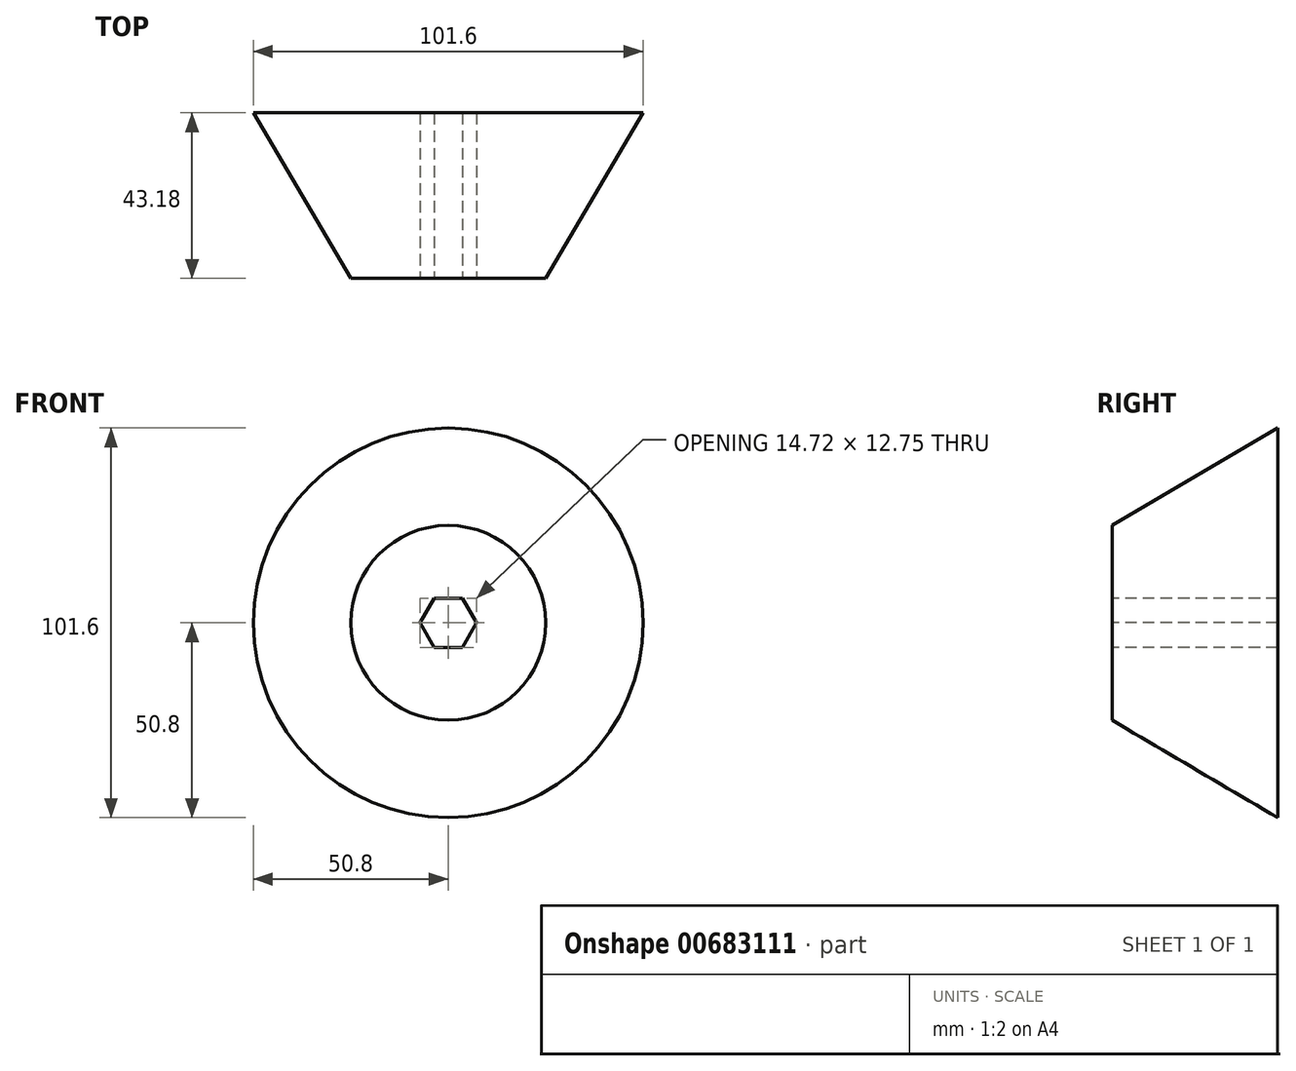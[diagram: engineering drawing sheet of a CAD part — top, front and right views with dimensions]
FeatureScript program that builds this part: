
annotation { "Feature Type Name" : "Feature", "Feature Type Description" : "" }
export const myFeature = defineFeature(function(context is Context, id is Id, definition is map)
    precondition{}
    {
        {
            var Q0;
            Q0=qCreatedBy(makeId("Front.planeOp"),FACE);
            var sketch = newSketch(context, id + "F0", { "sketchPlane" : qUnion([Q0])});
            skCircle(sketch, "E0", {"center": v(0, 0) * mm, "radius": 50.8 * mm});
            skSolve(sketch);
        }
        {
            var Q0;
            Q0=makeQuery(id+"F0.imprint","IMPRINT",FACE,{"disambiguationData":[TD([[makeQuery(id+"F0.imprint","IMPRINT",EDGE,{"derivedFrom":sQuery(id+"F0.wireOp",EDGE,"E0")}),1.0]])]});
            cPlane(context, id + "F1", {"entities" : qUnion([Q0]), "cplaneType" : CPlaneType.OFFSET, "offset" : 43.18 * mm, "width" : 152.4 * mm, "height" : 152.4 * mm});
        }
        {
            var Q0;
            Q0=qCreatedBy(id+"F1.planeOp",FACE);
            var sketch = newSketch(context, id + "F2", { "sketchPlane" : qUnion([Q0])});
            skCircle(sketch, "E1", {"center": v(0, 0) * mm, "radius": 25.4 * mm});
            skSolve(sketch);
        }
        {
            var Q0;
            Q0=makeQuery(id+"F0.imprint","IMPRINT",FACE,{"disambiguationData":[TD([[makeQuery(id+"F0.imprint","IMPRINT",EDGE,{"derivedFrom":sQuery(id+"F0.wireOp",EDGE,"E0")}),1.0]])]});
            var Q1;
            Q1=makeQuery(id+"F2.imprint","IMPRINT",FACE,{"disambiguationData":[TD([[makeQuery(id+"F2.imprint","IMPRINT",EDGE,{"derivedFrom":sQuery(id+"F2.wireOp",EDGE,"E1")}),1.0]])]});
            loft(context, id + "F3", {"sheetProfilesArray" : [{ "sheetProfileEntities" : qUnion([Q0]) }, { "sheetProfileEntities" : qUnion([Q1]) }]});
        }
        {
            var Q0;
            Q0=makeQuery(id+"F3.opLoft","CAP_FACE",FACE,{"disambiguationData":[OSD([makeQuery(id+"F2.imprint","IMPRINT",FACE,{"disambiguationData":[TD([[makeQuery(id+"F2.imprint","IMPRINT",EDGE,{"derivedFrom":sQuery(id+"F2.wireOp",EDGE,"E1")}),1.0]])]})])],"isStart":true});
            var sketch = newSketch(context, id + "F4", { "sketchPlane" : qUnion([Q0])});
            skCircle(sketch, "E2.cCircle", {"center": v(0, 0) * mm, "radius": 6.38 * mm, "construction": true});
            skLineSegment(sketch, "E2.0", {"start": v(3.68, -6.38) * mm, "end": v(-3.68, -6.38) * mm});
            skLineSegment(sketch, "E2.1", {"start": v(-3.68, -6.38) * mm, "end": v(-7.36, 0) * mm});
            skLineSegment(sketch, "E2.2", {"start": v(-7.36, 0) * mm, "end": v(-3.68, 6.38) * mm});
            skLineSegment(sketch, "E2.3", {"start": v(-3.68, 6.38) * mm, "end": v(3.68, 6.38) * mm});
            skLineSegment(sketch, "E2.4", {"start": v(3.68, 6.38) * mm, "end": v(7.36, 0) * mm});
            skLineSegment(sketch, "E2.5", {"start": v(7.36, 0) * mm, "end": v(3.68, -6.38) * mm});
            skPoint(sketch, "E2.0.midPoint", {"position": v(0, -6.38) * mm});
            skSolve(sketch);
        }
        {
            var Q0;
            Q0=makeQuery(id+"F4.imprint","IMPRINT",FACE,{"disambiguationData":[TD([[makeQuery(id+"F4.imprint","IMPRINT",EDGE,{"derivedFrom":sQuery(id+"F4.wireOp",EDGE,"E2.0")}),-1.0]])]});
            extrude(context, id + "F5", {"entities" : qUnion([Q0]), "operationType" : NewBodyOperationType.REMOVE, "oppositeDirection" : true, "depth" : 60.7 * mm, "offsetDistance" : 25.4 * mm});
        }
    });
